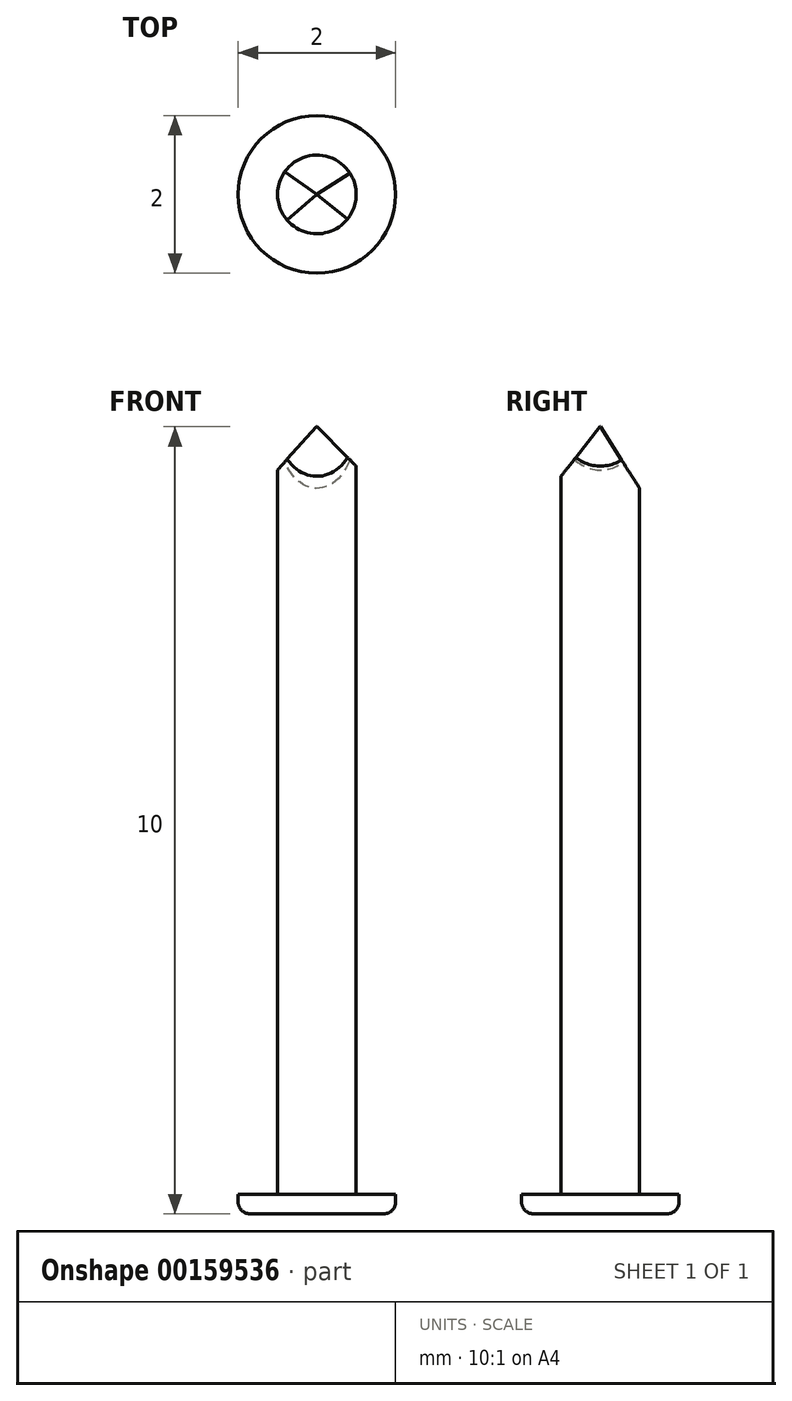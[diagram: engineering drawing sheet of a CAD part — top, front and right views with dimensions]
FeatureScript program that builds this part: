
annotation { "Feature Type Name" : "Feature", "Feature Type Description" : "" }
export const myFeature = defineFeature(function(context is Context, id is Id, definition is map)
    precondition{}
    {
        {
            var Q0;
            Q0=qCreatedBy(makeId("Top.planeOp"),FACE);
            var sketch = newSketch(context, id + "F0", { "sketchPlane" : qUnion([Q0])});
            skCircle(sketch, "E0", {"center": v(0, 0) * mm, "radius": 1 * mm});
            skCircle(sketch, "E1", {"center": v(0, 0) * mm, "radius": 0.5 * mm});
            skSolve(sketch);
        }
        {
            var Q0;
            Q0=makeQuery(id+"F0.imprint","IMPRINT",FACE,{"disambiguationData":[TD([[makeQuery(id+"F0.imprint","IMPRINT",EDGE,{"derivedFrom":sQuery(id+"F0.wireOp",EDGE,"E1")}),1.0]])]});
            extrude(context, id + "F1", {"entities" : qUnion([Q0]), "depth" : 10 * mm});
        }
        {
            var Q0;
            Q0=makeQuery(id+"F0.imprint","IMPRINT",FACE,{"disambiguationData":[TD([[makeQuery(id+"F0.imprint","IMPRINT",EDGE,{"derivedFrom":sQuery(id+"F0.wireOp",EDGE,"E0")}),1.0]])]});
            extrude(context, id + "F2", {"entities" : qUnion([Q0]), "operationType" : NewBodyOperationType.ADD, "depth" : 0.25 * mm});
        }
        {
            var Q0;
            Q0=makeQuery(id+"F2.opExtrude","CAP_EDGE",EDGE,{"disambiguationData":[OSD([sQuery(id+"F0.wireOp",EDGE,"E0")])],"isStart":true});
            fillet(context, id + "F3", {"entities" : qUnion([Q0]), "radius" : 0.15 * mm, "tangentPropagation" : true, "allowEdgeOverflow" : false});
        }
        {
            var Q0;
            Q0=qCreatedBy(makeId("Right.planeOp"),FACE);
            var sketch = newSketch(context, id + "F4", { "sketchPlane" : qUnion([Q0])});
            skLineSegment(sketch, "E2", {"start": v(0, 10) * mm, "end": v(0.56, 9.13) * mm});
            skLineSegment(sketch, "E3", {"start": v(0.56, 9.13) * mm, "end": v(0.56, 10.28) * mm});
            skLineSegment(sketch, "E4", {"start": v(-0.64, 10.28) * mm, "end": v(0.56, 10.28) * mm});
            skLineSegment(sketch, "E5", {"start": v(-0.64, 10.28) * mm, "end": v(-0.64, 9.19) * mm});
            skLineSegment(sketch, "E6", {"start": v(-0.64, 9.19) * mm, "end": v(0, 10) * mm});
            skSolve(sketch);
        }
        {
            var Q0;
            Q0 = qSketchRegion(id + "F4", true);
            extrude(context, id + "F5", {"entities" : qUnion([Q0]), "operationType" : NewBodyOperationType.REMOVE, "depth" : 25 * mm, "hasSecondDirection" : true, "secondDirectionOppositeDirection" : true, "secondDirectionDepth" : 25 * mm});
        }
        {
            var Q0;
            Q0=qCreatedBy(makeId("Front.planeOp"),FACE);
            var sketch = newSketch(context, id + "F6", { "sketchPlane" : qUnion([Q0])});
            skLineSegment(sketch, "E7", {"start": v(0, 10) * mm, "end": v(-0.58, 9.36) * mm});
            skLineSegment(sketch, "E8", {"start": v(-0.58, 9.36) * mm, "end": v(-0.58, 10.16) * mm});
            skLineSegment(sketch, "E9", {"start": v(-0.58, 10.16) * mm, "end": v(0.6, 10.16) * mm});
            skLineSegment(sketch, "E10", {"start": v(0.6, 10.16) * mm, "end": v(0.6, 9.4) * mm});
            skLineSegment(sketch, "E11", {"start": v(0.6, 9.4) * mm, "end": v(0, 10) * mm});
            skSolve(sketch);
        }
        {
            var Q0;
            Q0 = qSketchRegion(id + "F6", true);
            extrude(context, id + "F7", {"entities" : qUnion([Q0]), "operationType" : NewBodyOperationType.REMOVE, "depth" : 25 * mm, "hasSecondDirection" : true, "secondDirectionOppositeDirection" : true, "secondDirectionDepth" : 25 * mm});
        }
    });
